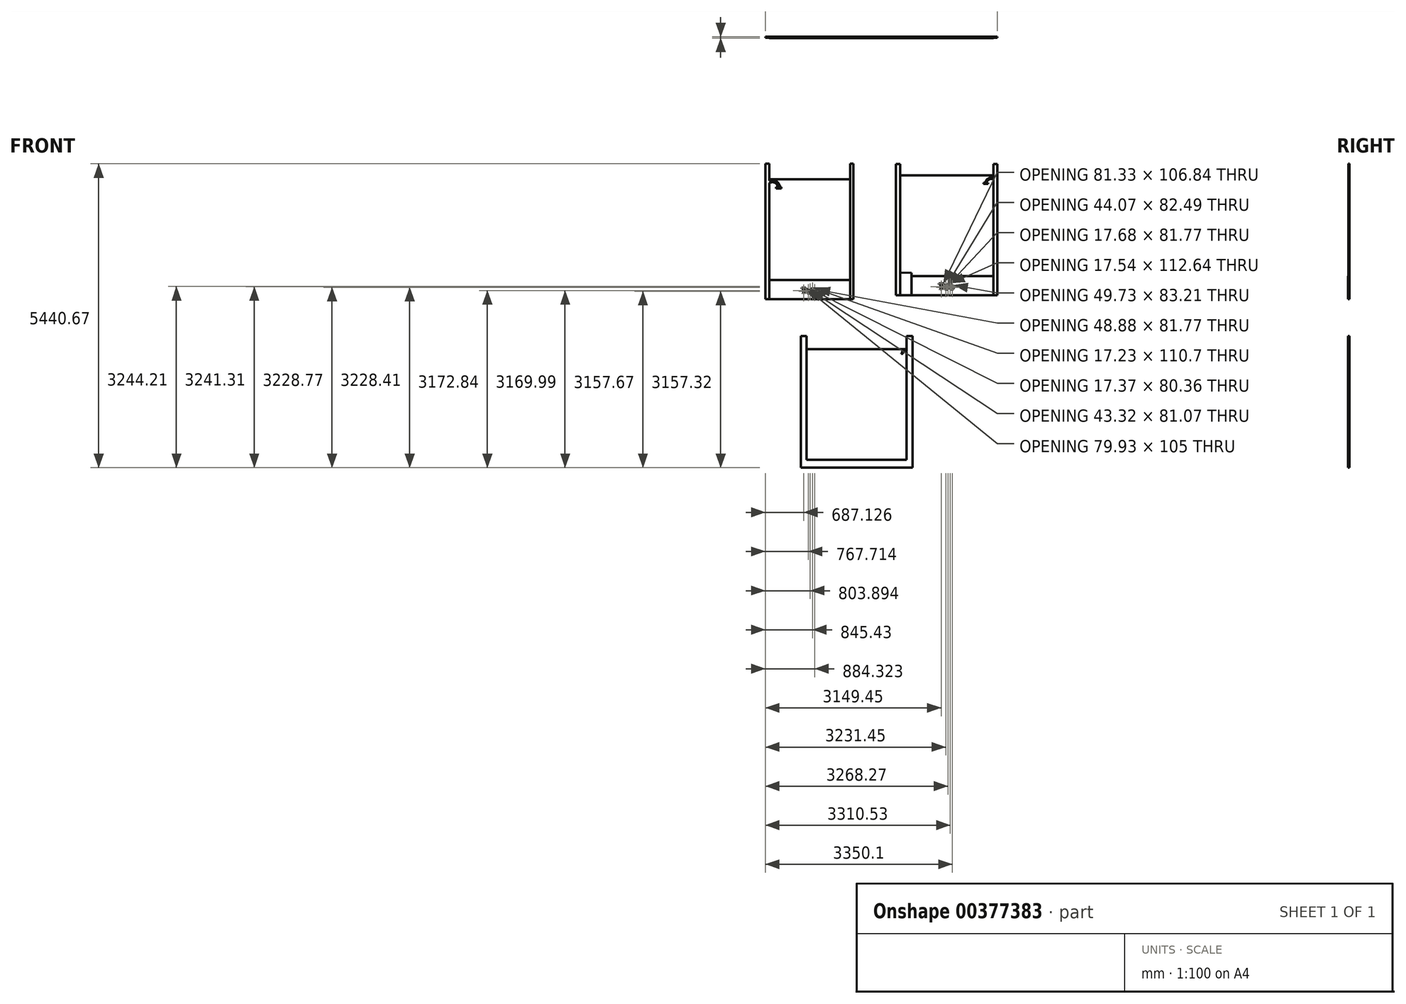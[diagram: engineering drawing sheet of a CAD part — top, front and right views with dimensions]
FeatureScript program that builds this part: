
annotation { "Feature Type Name" : "Feature", "Feature Type Description" : "" }
export const myFeature = defineFeature(function(context is Context, id is Id, definition is map)
    precondition{}
    {
        {
            var Q0;
            Q0=qCreatedBy(makeId("Front.planeOp"),FACE);
            var sketch = newSketch(context, id + "F0", { "sketchPlane" : qUnion([Q0])});
            skLineSegment(sketch, "E0.bottom", {"start": v(0, 0) * mm, "end": v(1447.8, 0) * mm});
            skLineSegment(sketch, "E0.top", {"start": v(0, 339.72) * mm, "end": v(1447.8, 339.72) * mm});
            skLineSegment(sketch, "E0.left", {"start": v(0, 0) * mm, "end": v(0, 339.72) * mm});
            skLineSegment(sketch, "E0.right", {"start": v(1447.8, 0) * mm, "end": v(1447.8, 339.72) * mm});
            skLineSegment(sketch, "E1", {"start": v(0, 339.72) * mm, "end": v(0, 2421.38) * mm});
            skLineSegment(sketch, "E2", {"start": v(1447.8, 339.72) * mm, "end": v(1447.8, 2421.38) * mm});
            skText(sketch, "E3", { "text": "Tub", "fontName": "AllertaStencil-Regular.ttf"});
            skLineSegment(sketch, "E4.bottom", {"start": v(0, 2421.38) * mm, "end": v(-73.56, 2421.38) * mm});
            skLineSegment(sketch, "E4.top", {"start": v(0, 0) * mm, "end": v(-73.56, 0) * mm});
            skLineSegment(sketch, "E4.left", {"start": v(0, 2421.38) * mm, "end": v(0, 0) * mm});
            skLineSegment(sketch, "E4.right", {"start": v(-73.56, 2421.38) * mm, "end": v(-73.56, 0) * mm});
            skLineSegment(sketch, "E5.bottom", {"start": v(1447.8, 2421.38) * mm, "end": v(1502.85, 2421.38) * mm});
            skLineSegment(sketch, "E5.top", {"start": v(1447.8, 0) * mm, "end": v(1502.85, 0) * mm});
            skLineSegment(sketch, "E5.left", {"start": v(1447.8, 2421.38) * mm, "end": v(1447.8, 0) * mm});
            skLineSegment(sketch, "E5.right", {"start": v(1502.85, 2421.38) * mm, "end": v(1502.85, 0) * mm});
            skArc(sketch, "E6", {"start": v(189.2, 2002.48) * mm, "mid": v(124.8, 2109.76) * mm, "end": v(0, 2118.8) * mm});
            skArc(sketch, "E7.0", {"start": v(150.9, 2003.6) * mm, "mid": v(95.8, 2082.23) * mm, "end": v(0, 2075.69) * mm});
            skLineSegment(sketch, "E8.bottom", {"start": v(118.31, 2003.6) * mm, "end": v(215.5, 2003.6) * mm});
            skLineSegment(sketch, "E8.top", {"start": v(118.31, 1981.63) * mm, "end": v(215.5, 1981.63) * mm});
            skLineSegment(sketch, "E8.left", {"start": v(118.31, 2003.6) * mm, "end": v(118.31, 1981.63) * mm});
            skLineSegment(sketch, "E8.right", {"start": v(215.5, 2003.6) * mm, "end": v(215.5, 1981.63) * mm});
            skLineSegment(sketch, "E9.top", {"start": v(0, 2143.12) * mm, "end": v(1447.8, 2143.12) * mm});
            skLineSegment(sketch, "E9.left", {"start": v(0, 339.72) * mm, "end": v(0, 2143.12) * mm});
            skLineSegment(sketch, "E9.right", {"start": v(1447.8, 339.72) * mm, "end": v(1447.8, 2143.12) * mm});
            const initialGuessF0  = {"E3": [0.56633, 0.0982, 1, 0, 0.10505]};
            skSetInitialGuess(sketch, initialGuessF0);
            skSolve(sketch);
        }
        {
            var Q0;
            Q0=makeQuery(id+"F0.imprint","IMPRINT",FACE,{"disambiguationData":[TD([[makeQuery(id+"F0.imprint","IMPRINT",EDGE,{"derivedFrom":sQuery(id+"F0.wireOp",EDGE,"E0.bottom")}),1.0]])]});
            extrude(context, id + "F1", {"entities" : qUnion([Q0]), "depth" : 25.4 * mm});
        }
        {
            var Q0;
            {var subQ3=sQuery(id+"F0.wireOp",EDGE,"E4.bottom");Q0=makeQuery(id+"F0.imprint","IMPRINT",FACE,{"disambiguationData":[TD([[makeQuery(id+"F0.imprint","IMPRINT",EDGE,{"derivedFrom":subQ3}),1.0]])]});}
            var Q1;
            {var subQ3=sQuery(id+"F0.wireOp",EDGE,"E5.bottom");Q1=makeQuery(id+"F0.imprint","IMPRINT",FACE,{"disambiguationData":[TD([[makeQuery(id+"F0.imprint","IMPRINT",EDGE,{"derivedFrom":subQ3}),-1.0]])]});}
            var Q2;
            {var subQ5=sQuery(id+"F0.wireOp",EDGE,"E7.0");Q2=makeQuery(id+"F0.imprint","IMPRINT",FACE,{"disambiguationData":[TD([[makeQuery(id+"F0.imprint","IMPRINT",EDGE,{"derivedFrom":subQ5}),-1.0]])]});}
            var Q3;
            Q3=makeQuery(id+"F0.imprint","IMPRINT",FACE,{"disambiguationData":[TD([[makeQuery(id+"F0.imprint","IMPRINT",EDGE,{"derivedFrom":sQuery(id+"F0.wireOp",EDGE,"E8.top")}),1.0]])]});
            extrude(context, id + "F2", {"entities" : qUnion([Q0, Q1, Q2, Q3]), "operationType" : NewBodyOperationType.ADD, "depth" : 20.32 * mm});
        }
        {
            var Q0;
            {var subQ1=sQuery(id+"F0.wireOp",EDGE,"E7.0");Q0=makeQuery(id+"F0.imprint","IMPRINT",FACE,{"disambiguationData":[TD([[makeQuery(id+"F0.imprint","IMPRINT",EDGE,{"derivedFrom":subQ1}),1.0]])]});}
            extrude(context, id + "F3", {"entities" : qUnion([Q0]), "operationType" : NewBodyOperationType.ADD, "depth" : 12.7 * mm});
        }
        {
            var Q0;
            Q0=qCreatedBy(makeId("Front.planeOp"),FACE);
            var sketch = newSketch(context, id + "F4", { "sketchPlane" : qUnion([Q0])});
            skLineSegment(sketch, "E10.bottom", {"start": v(2542.57, 68.69) * mm, "end": v(4012.6, 68.69) * mm});
            skLineSegment(sketch, "E10.top", {"start": v(2542.57, 408.41) * mm, "end": v(4012.6, 408.41) * mm});
            skLineSegment(sketch, "E10.left", {"start": v(2542.57, 68.69) * mm, "end": v(2542.57, 408.41) * mm});
            skLineSegment(sketch, "E10.right", {"start": v(4012.6, 68.69) * mm, "end": v(4012.6, 408.41) * mm});
            skLineSegment(sketch, "E11", {"start": v(4012.6, 408.41) * mm, "end": v(4012.6, 2416.76) * mm});
            skText(sketch, "E12", { "text": "Tub", "fontName": "AllertaStencil-Regular.ttf"});
            skLineSegment(sketch, "E13.bottom", {"start": v(4012.6, 2416.76) * mm, "end": v(4078.17, 2416.76) * mm});
            skLineSegment(sketch, "E13.top", {"start": v(4012.6, 68.69) * mm, "end": v(4078.17, 68.69) * mm});
            skLineSegment(sketch, "E13.left", {"start": v(4012.6, 2416.76) * mm, "end": v(4012.6, 68.69) * mm});
            skLineSegment(sketch, "E13.right", {"start": v(4078.17, 2416.76) * mm, "end": v(4078.17, 68.69) * mm});
            skLineSegment(sketch, "E14.bottom", {"start": v(2542.57, 68.69) * mm, "end": v(2342.54, 68.69) * mm});
            skLineSegment(sketch, "E14.left", {"start": v(2542.57, 68.69) * mm, "end": v(2542.57, 468.74) * mm});
            skLineSegment(sketch, "E14.right", {"start": v(2342.54, 68.69) * mm, "end": v(2342.54, 475.09) * mm});
            skLineSegment(sketch, "E15.bottom", {"start": v(2342.54, 68.69) * mm, "end": v(2263.37, 68.69) * mm});
            skLineSegment(sketch, "E15.top", {"start": v(2342.54, 2416.76) * mm, "end": v(2263.37, 2416.76) * mm});
            skLineSegment(sketch, "E15.left", {"start": v(2342.54, 68.69) * mm, "end": v(2342.54, 2416.76) * mm});
            skLineSegment(sketch, "E15.right", {"start": v(2263.37, 68.69) * mm, "end": v(2263.37, 2416.76) * mm});
            skArc(sketch, "E16", {"start": v(4012.6, 2148.37) * mm, "mid": v(3935.36, 2142.01) * mm, "end": v(3886.74, 2081.66) * mm});
            skArc(sketch, "E17.0", {"start": v(4012.6, 2172.49) * mm, "mid": v(3918.3, 2158.9) * mm, "end": v(3862.86, 2081.43) * mm});
            skLineSegment(sketch, "E18.bottom", {"start": v(3916.27, 2081.66) * mm, "end": v(3834.97, 2081.66) * mm});
            skLineSegment(sketch, "E18.top", {"start": v(3916.27, 2060.7) * mm, "end": v(3834.97, 2060.7) * mm});
            skLineSegment(sketch, "E18.left", {"start": v(3916.27, 2081.66) * mm, "end": v(3916.27, 2060.7) * mm});
            skLineSegment(sketch, "E18.right", {"start": v(3834.97, 2081.66) * mm, "end": v(3834.97, 2060.7) * mm});
            skLineSegment(sketch, "E19", {"start": v(2542.57, 468.74) * mm, "end": v(2342.54, 475.09) * mm});
            skLineSegment(sketch, "E20", {"start": v(3277.58, 408.41) * mm, "end": v(3277.58, 2211.81) * mm, "construction": true});
            skLineSegment(sketch, "E21", {"start": v(2342.54, 2211.81) * mm, "end": v(4012.6, 2211.81) * mm});
            const initialGuessF4  = {"E12": [3.02783, 0.1686, 1, 0, 0.10689]};
            skSetInitialGuess(sketch, initialGuessF4);
            skSolve(sketch);
        }
        {
            var Q0;
            {var subQ0=sQuery(id+"F4.wireOp",EDGE,"E10.bottom");Q0=makeQuery(id+"F4.imprint","IMPRINT",FACE,{"disambiguationData":[TD([[makeQuery(id+"F4.imprint","IMPRINT",EDGE,{"derivedFrom":subQ0}),1.0]])]});}
            extrude(context, id + "F5", {"entities" : qUnion([Q0]), "depth" : 25.4 * mm});
        }
        {
            var Q0;
            {var subQ3=sQuery(id+"F4.wireOp",EDGE,"E14.bottom");Q0=makeQuery(id+"F4.imprint","IMPRINT",FACE,{"disambiguationData":[TD([[makeQuery(id+"F4.imprint","IMPRINT",EDGE,{"derivedFrom":subQ3}),-1.0]])]});}
            extrude(context, id + "F6", {"entities" : qUnion([Q0]), "operationType" : NewBodyOperationType.ADD, "depth" : 22.86 * mm});
        }
        {
            var Q0;
            {var subQ3=sQuery(id+"F4.wireOp",EDGE,"E15.bottom");Q0=makeQuery(id+"F4.imprint","IMPRINT",FACE,{"disambiguationData":[TD([[makeQuery(id+"F4.imprint","IMPRINT",EDGE,{"derivedFrom":subQ3}),-1.0]])]});}
            var Q1;
            {var subQ3=sQuery(id+"F4.wireOp",EDGE,"E13.bottom");Q1=makeQuery(id+"F4.imprint","IMPRINT",FACE,{"disambiguationData":[TD([[makeQuery(id+"F4.imprint","IMPRINT",EDGE,{"derivedFrom":subQ3}),-1.0]])]});}
            extrude(context, id + "F7", {"entities" : qUnion([Q0, Q1]), "operationType" : NewBodyOperationType.ADD, "depth" : 20.32 * mm});
        }
        {
            var Q0;
            {var subQ0=sQuery(id+"F4.wireOp",EDGE,"E16");Q0=makeQuery(id+"F4.imprint","IMPRINT",FACE,{"disambiguationData":[TD([[makeQuery(id+"F4.imprint","IMPRINT",EDGE,{"derivedFrom":subQ0}),-1.0]])]});}
            var Q1;
            Q1=makeQuery(id+"F4.imprint","IMPRINT",FACE,{"disambiguationData":[TD([[makeQuery(id+"F4.imprint","IMPRINT",EDGE,{"derivedFrom":sQuery(id+"F4.wireOp",EDGE,"E18.top")}),-1.0]])]});
            extrude(context, id + "F8", {"entities" : qUnion([Q0, Q1]), "operationType" : NewBodyOperationType.ADD, "depth" : 17.78 * mm});
        }
        {
            var Q0;
            {var subQ10=sQuery(id+"F4.wireOp",EDGE,"E10.top");Q0=makeQuery(id+"F4.imprint","IMPRINT",FACE,{"disambiguationData":[TD([[makeQuery(id+"F4.imprint","IMPRINT",EDGE,{"derivedFrom":subQ10}),1.0]])]});}
            extrude(context, id + "F9", {"entities" : qUnion([Q0]), "operationType" : NewBodyOperationType.ADD, "depth" : 12.7 * mm});
        }
        {
            var Q0;
            Q0=qCreatedBy(makeId("Front.planeOp"),FACE);
            var sketch = newSketch(context, id + "F10", { "sketchPlane" : qUnion([Q0])});
            skLineSegment(sketch, "E22.bottom", {"start": v(666.79, -2879.59) * mm, "end": v(2457.49, -2879.59) * mm});
            skLineSegment(sketch, "E22.top", {"start": v(666.79, -3019.29) * mm, "end": v(2457.49, -3019.29) * mm});
            skLineSegment(sketch, "E22.left", {"start": v(666.79, -2879.59) * mm, "end": v(666.79, -3019.29) * mm});
            skLineSegment(sketch, "E22.right", {"start": v(2457.49, -2879.59) * mm, "end": v(2457.49, -3019.29) * mm});
            skLineSegment(sketch, "E23.bottom", {"start": v(2457.49, -3019.29) * mm, "end": v(2559.5, -3019.29) * mm});
            skLineSegment(sketch, "E23.top", {"start": v(2457.49, -662.41) * mm, "end": v(2559.5, -662.41) * mm});
            skLineSegment(sketch, "E23.left", {"start": v(2457.49, -3019.29) * mm, "end": v(2457.49, -662.41) * mm});
            skLineSegment(sketch, "E23.right", {"start": v(2559.5, -3019.29) * mm, "end": v(2559.5, -662.41) * mm});
            skLineSegment(sketch, "E24.bottom", {"start": v(666.79, -3019.29) * mm, "end": v(564.76, -3019.29) * mm});
            skLineSegment(sketch, "E24.top", {"start": v(666.79, -662.41) * mm, "end": v(564.76, -662.41) * mm});
            skLineSegment(sketch, "E24.left", {"start": v(666.79, -3019.29) * mm, "end": v(666.79, -662.41) * mm});
            skLineSegment(sketch, "E24.right", {"start": v(564.76, -3019.29) * mm, "end": v(564.76, -662.41) * mm});
            skArc(sketch, "E25", {"start": v(2457.49, -935.43) * mm, "mid": v(2400.47, -922.54) * mm, "end": v(2369.36, -972.03) * mm});
            skArc(sketch, "E26.0", {"start": v(2457.49, -964.74) * mm, "mid": v(2416.22, -931.54) * mm, "end": v(2382.08, -972.03) * mm});
            skLineSegment(sketch, "E27.bottom", {"start": v(2388.8, -972.03) * mm, "end": v(2360.3, -972.03) * mm});
            skLineSegment(sketch, "E27.top", {"start": v(2388.8, -978.08) * mm, "end": v(2360.3, -978.08) * mm});
            skLineSegment(sketch, "E27.left", {"start": v(2388.8, -972.03) * mm, "end": v(2388.8, -978.08) * mm});
            skLineSegment(sketch, "E27.right", {"start": v(2360.3, -972.03) * mm, "end": v(2360.3, -978.08) * mm});
            skLineSegment(sketch, "E28.top", {"start": v(666.79, -898.39) * mm, "end": v(2457.49, -898.39) * mm});
            skLineSegment(sketch, "E28.left", {"start": v(666.79, -2879.59) * mm, "end": v(666.79, -898.39) * mm});
            skLineSegment(sketch, "E28.right", {"start": v(2457.49, -2879.59) * mm, "end": v(2457.49, -898.39) * mm});
            skSolve(sketch);
        }
        {
            var Q0;
            {var subQ3=sQuery(id+"F10.wireOp",EDGE,"E24.bottom");Q0=makeQuery(id+"F10.imprint","IMPRINT",FACE,{"disambiguationData":[TD([[makeQuery(id+"F10.imprint","IMPRINT",EDGE,{"derivedFrom":subQ3}),-1.0]])]});}
            var Q1;
            {var subQ3=sQuery(id+"F10.wireOp",EDGE,"E23.bottom");Q1=makeQuery(id+"F10.imprint","IMPRINT",FACE,{"disambiguationData":[TD([[makeQuery(id+"F10.imprint","IMPRINT",EDGE,{"derivedFrom":subQ3}),1.0]])]});}
            var Q2;
            {var subQ0=sQuery(id+"F10.wireOp",EDGE,"E25");Q2=makeQuery(id+"F10.imprint","IMPRINT",FACE,{"disambiguationData":[TD([[makeQuery(id+"F10.imprint","IMPRINT",EDGE,{"derivedFrom":subQ0}),1.0]])]});}
            var Q3;
            Q3=makeQuery(id+"F10.imprint","IMPRINT",FACE,{"disambiguationData":[TD([[makeQuery(id+"F10.imprint","IMPRINT",EDGE,{"derivedFrom":sQuery(id+"F10.wireOp",EDGE,"E27.top")}),-1.0]])]});
            var Q4;
            {var subQ0=sQuery(id+"F10.wireOp",EDGE,"E22.bottom");Q4=makeQuery(id+"F10.imprint","IMPRINT",FACE,{"disambiguationData":[TD([[makeQuery(id+"F10.imprint","IMPRINT",EDGE,{"derivedFrom":subQ0}),-1.0]])]});}
            var Q5;
            {var subQ0=sQuery(id+"F10.wireOp",EDGE,"E22.top");Q5=makeQuery(id+"F10.imprint","IMPRINT",FACE,{"disambiguationData":[TD([[makeQuery(id+"F10.imprint","IMPRINT",EDGE,{"derivedFrom":subQ0}),1.0]])]});}
            extrude(context, id + "F11", {"entities" : qUnion([Q0, Q1, Q2, Q3, Q4, Q5]), "depth" : 25.4 * mm});
        }
        {
            var Q0;
            {var subQ4=sQuery(id+"F10.wireOp",EDGE,"E25");Q0=makeQuery(id+"F10.imprint","IMPRINT",FACE,{"disambiguationData":[TD([[makeQuery(id+"F10.imprint","IMPRINT",EDGE,{"derivedFrom":subQ4}),-1.0]])]});}
            extrude(context, id + "F12", {"entities" : qUnion([Q0]), "operationType" : NewBodyOperationType.ADD, "depth" : 12.7 * mm});
        }
    });
